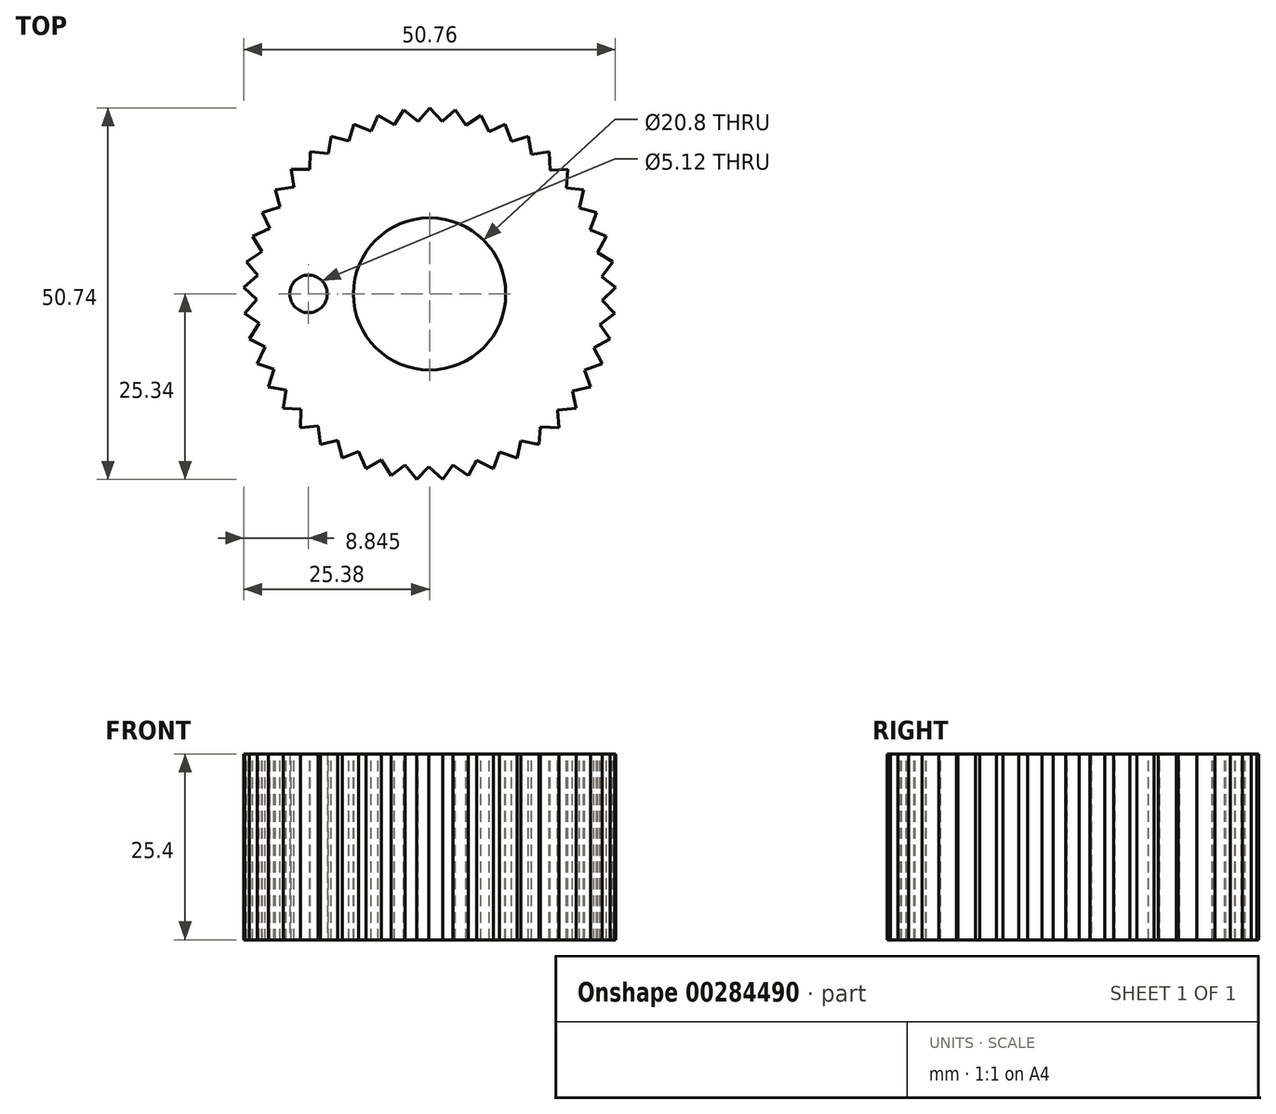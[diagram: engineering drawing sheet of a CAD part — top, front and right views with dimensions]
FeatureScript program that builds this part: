
annotation { "Feature Type Name" : "Feature", "Feature Type Description" : "" }
export const myFeature = defineFeature(function(context is Context, id is Id, definition is map)
    precondition{}
    {
        {
            var Q0;
            Q0=qCreatedBy(makeId("Top.planeOp"),FACE);
            var sketch = newSketch(context, id + "F0", { "sketchPlane" : qUnion([Q0])});
            skCircle(sketch, "E0", {"center": v(0, 0) * mm, "radius": 25.4 * mm});
            skSolve(sketch);
        }
        {
            var Q0;
            Q0=makeQuery(id+"F0.imprint","IMPRINT",FACE,{"disambiguationData":[TD([[makeQuery(id+"F0.imprint","IMPRINT",EDGE,{"derivedFrom":sQuery(id+"F0.wireOp",EDGE,"E0")}),1.0]])]});
            extrude(context, id + "F1", {"entities" : qUnion([Q0]), "depth" : 25.4 * mm});
        }
        {
            var Q0;
            Q0=makeQuery(id+"F1.opExtrude","CAP_FACE",FACE,{"disambiguationData":[OSD([sQuery(id+"F0.wireOp",EDGE,"E0")])],"isStart":false});
            var sketch = newSketch(context, id + "F2", { "sketchPlane" : qUnion([Q0])});
            skLineSegment(sketch, "E1", {"start": v(0, 0) * mm, "end": v(0, 49.68) * mm});
            skLineSegment(sketch, "E2", {"start": v(0, 24.84) * mm, "end": v(0, 25.4) * mm});
            skLineSegment(sketch, "E3", {"start": v(0, 25.4) * mm, "end": v(2.47, 22.76) * mm});
            skLineSegment(sketch, "E4", {"start": v(2.47, 22.76) * mm, "end": v(-2.23, 22.76) * mm});
            skLineSegment(sketch, "E5", {"start": v(-2.23, 22.76) * mm, "end": v(0, 25.4) * mm});
            skCircle(sketch, "E6.0", {"center": v(0, 0) * mm, "radius": 25.4 * mm});
            skLineSegment(sketch, "E7.1.1", {"start": v(-3.53, 25.15) * mm, "end": v(-0.72, 22.88) * mm});
            skLineSegment(sketch, "E7.1.2", {"start": v(-0.72, 22.88) * mm, "end": v(-5.38, 22.23) * mm});
            skLineSegment(sketch, "E7.1.3", {"start": v(-5.38, 22.23) * mm, "end": v(-3.53, 25.15) * mm});
            skLineSegment(sketch, "E7.2.1", {"start": v(-7, 24.42) * mm, "end": v(-3.9, 22.56) * mm});
            skLineSegment(sketch, "E7.2.2", {"start": v(-3.9, 22.56) * mm, "end": v(-8.42, 21.26) * mm});
            skLineSegment(sketch, "E7.2.3", {"start": v(-8.42, 21.26) * mm, "end": v(-7, 24.42) * mm});
            skLineSegment(sketch, "E8.2.3.0", {"start": v(-10.33, 23.2) * mm, "end": v(-7, 21.8) * mm});
            skLineSegment(sketch, "E8.5.3.0", {"start": v(-7, 21.8) * mm, "end": v(-11.3, 19.88) * mm});
            skLineSegment(sketch, "E8.8.3.0", {"start": v(-11.3, 19.88) * mm, "end": v(-10.33, 23.2) * mm});
            skLineSegment(sketch, "E8.2.4.0", {"start": v(-13.46, 21.54) * mm, "end": v(-9.96, 20.6) * mm});
            skLineSegment(sketch, "E8.5.4.0", {"start": v(-9.96, 20.6) * mm, "end": v(-13.96, 18.12) * mm});
            skLineSegment(sketch, "E8.8.4.0", {"start": v(-13.96, 18.12) * mm, "end": v(-13.46, 21.54) * mm});
            skLineSegment(sketch, "E8.2.5.0", {"start": v(-16.33, 19.46) * mm, "end": v(-12.74, 19.02) * mm});
            skLineSegment(sketch, "E8.5.5.0", {"start": v(-12.74, 19.02) * mm, "end": v(-16.34, 16) * mm});
            skLineSegment(sketch, "E8.8.5.0", {"start": v(-16.34, 16) * mm, "end": v(-16.33, 19.46) * mm});
            skLineSegment(sketch, "E8.2.6.0", {"start": v(-18.88, 17) * mm, "end": v(-15.26, 17.06) * mm});
            skLineSegment(sketch, "E8.5.6.0", {"start": v(-15.26, 17.06) * mm, "end": v(-18.4, 13.57) * mm});
            skLineSegment(sketch, "E8.8.6.0", {"start": v(-18.4, 13.57) * mm, "end": v(-18.88, 17) * mm});
            skLineSegment(sketch, "E8.2.7.0", {"start": v(-21.06, 14.2) * mm, "end": v(-17.49, 14.78) * mm});
            skLineSegment(sketch, "E8.5.7.0", {"start": v(-17.49, 14.78) * mm, "end": v(-20.12, 10.87) * mm});
            skLineSegment(sketch, "E8.8.7.0", {"start": v(-20.12, 10.87) * mm, "end": v(-21.06, 14.2) * mm});
            skLineSegment(sketch, "E8.2.8.0", {"start": v(-22.83, 11.13) * mm, "end": v(-19.37, 12.2) * mm});
            skLineSegment(sketch, "E8.5.8.0", {"start": v(-19.37, 12.2) * mm, "end": v(-21.43, 7.97) * mm});
            skLineSegment(sketch, "E8.8.8.0", {"start": v(-21.43, 7.97) * mm, "end": v(-22.83, 11.13) * mm});
            skLineSegment(sketch, "E8.2.9.0", {"start": v(-24.16, 7.85) * mm, "end": v(-20.88, 9.38) * mm});
            skLineSegment(sketch, "E8.5.9.0", {"start": v(-20.88, 9.38) * mm, "end": v(-22.34, 4.9) * mm});
            skLineSegment(sketch, "E8.8.9.0", {"start": v(-22.34, 4.9) * mm, "end": v(-24.16, 7.85) * mm});
            skLineSegment(sketch, "E8.2.10.0", {"start": v(-25.01, 4.41) * mm, "end": v(-21.98, 6.39) * mm});
            skLineSegment(sketch, "E8.5.10.0", {"start": v(-21.98, 6.39) * mm, "end": v(-22.8, 1.75) * mm});
            skLineSegment(sketch, "E8.8.10.0", {"start": v(-22.8, 1.75) * mm, "end": v(-25.01, 4.41) * mm});
            skLineSegment(sketch, "E8.2.11.0", {"start": v(-25.38, 0.89) * mm, "end": v(-22.66, 3.26) * mm});
            skLineSegment(sketch, "E8.5.11.0", {"start": v(-22.66, 3.26) * mm, "end": v(-22.82, -1.44) * mm});
            skLineSegment(sketch, "E8.8.11.0", {"start": v(-22.82, -1.44) * mm, "end": v(-25.38, 0.89) * mm});
            skLineSegment(sketch, "E8.2.12.0", {"start": v(-25.26, -2.66) * mm, "end": v(-22.9, 0.08) * mm});
            skLineSegment(sketch, "E8.5.12.0", {"start": v(-22.9, 0.08) * mm, "end": v(-22.4, -4.6) * mm});
            skLineSegment(sketch, "E8.8.12.0", {"start": v(-22.4, -4.6) * mm, "end": v(-25.26, -2.66) * mm});
            skLineSegment(sketch, "E8.2.13.0", {"start": v(-24.65, -6.14) * mm, "end": v(-22.68, -3.1) * mm});
            skLineSegment(sketch, "E8.5.13.0", {"start": v(-22.68, -3.1) * mm, "end": v(-21.54, -7.67) * mm});
            skLineSegment(sketch, "E8.8.13.0", {"start": v(-21.54, -7.67) * mm, "end": v(-24.65, -6.14) * mm});
            skLineSegment(sketch, "E8.2.14.0", {"start": v(-23.55, -9.52) * mm, "end": v(-22.03, -6.23) * mm});
            skLineSegment(sketch, "E8.5.14.0", {"start": v(-22.03, -6.23) * mm, "end": v(-20.26, -10.6) * mm});
            skLineSegment(sketch, "E8.8.14.0", {"start": v(-20.26, -10.6) * mm, "end": v(-23.55, -9.52) * mm});
            skLineSegment(sketch, "E8.2.15.0", {"start": v(-22, -12.7) * mm, "end": v(-20.95, -9.24) * mm});
            skLineSegment(sketch, "E8.5.15.0", {"start": v(-20.95, -9.24) * mm, "end": v(-18.6, -13.31) * mm});
            skLineSegment(sketch, "E8.8.15.0", {"start": v(-18.6, -13.31) * mm, "end": v(-22, -12.7) * mm});
            skLineSegment(sketch, "E8.2.16.0", {"start": v(-20.02, -15.64) * mm, "end": v(-19.46, -12.06) * mm});
            skLineSegment(sketch, "E8.5.16.0", {"start": v(-19.46, -12.06) * mm, "end": v(-16.56, -15.77) * mm});
            skLineSegment(sketch, "E8.8.16.0", {"start": v(-16.56, -15.77) * mm, "end": v(-20.02, -15.64) * mm});
            skLineSegment(sketch, "E8.2.17.0", {"start": v(-17.64, -18.27) * mm, "end": v(-17.59, -14.65) * mm});
            skLineSegment(sketch, "E8.5.17.0", {"start": v(-17.59, -14.65) * mm, "end": v(-14.2, -17.92) * mm});
            skLineSegment(sketch, "E8.8.17.0", {"start": v(-14.2, -17.92) * mm, "end": v(-17.64, -18.27) * mm});
            skLineSegment(sketch, "E8.2.18.0", {"start": v(-14.93, -20.55) * mm, "end": v(-15.38, -16.96) * mm});
            skLineSegment(sketch, "E8.5.18.0", {"start": v(-15.38, -16.96) * mm, "end": v(-11.57, -19.73) * mm});
            skLineSegment(sketch, "E8.8.18.0", {"start": v(-11.57, -19.73) * mm, "end": v(-14.93, -20.55) * mm});
            skLineSegment(sketch, "E8.2.19.0", {"start": v(-11.92, -22.43) * mm, "end": v(-12.87, -18.93) * mm});
            skLineSegment(sketch, "E8.5.19.0", {"start": v(-12.87, -18.93) * mm, "end": v(-8.71, -21.14) * mm});
            skLineSegment(sketch, "E8.8.19.0", {"start": v(-8.71, -21.14) * mm, "end": v(-11.92, -22.43) * mm});
            skLineSegment(sketch, "E8.2.20.0", {"start": v(-8.69, -23.87) * mm, "end": v(-10.1, -20.54) * mm});
            skLineSegment(sketch, "E8.5.20.0", {"start": v(-10.1, -20.54) * mm, "end": v(-5.68, -22.15) * mm});
            skLineSegment(sketch, "E8.8.20.0", {"start": v(-5.68, -22.15) * mm, "end": v(-8.69, -23.87) * mm});
            skLineSegment(sketch, "E8.2.21.0", {"start": v(-5.28, -24.84) * mm, "end": v(-7.15, -21.75) * mm});
            skLineSegment(sketch, "E8.5.21.0", {"start": v(-7.15, -21.75) * mm, "end": v(-2.55, -22.73) * mm});
            skLineSegment(sketch, "E8.8.21.0", {"start": v(-2.55, -22.73) * mm, "end": v(-5.28, -24.84) * mm});
            skLineSegment(sketch, "E8.2.22.0", {"start": v(-1.77, -25.34) * mm, "end": v(-4.05, -22.53) * mm});
            skLineSegment(sketch, "E8.5.22.0", {"start": v(-4.05, -22.53) * mm, "end": v(0.64, -22.86) * mm});
            skLineSegment(sketch, "E8.8.22.0", {"start": v(0.64, -22.86) * mm, "end": v(-1.77, -25.34) * mm});
            skLineSegment(sketch, "E8.2.23.0", {"start": v(1.77, -25.34) * mm, "end": v(-0.88, -22.88) * mm});
            skLineSegment(sketch, "E8.5.23.0", {"start": v(-0.88, -22.88) * mm, "end": v(3.82, -22.55) * mm});
            skLineSegment(sketch, "E8.8.23.0", {"start": v(3.82, -22.55) * mm, "end": v(1.77, -25.34) * mm});
            skLineSegment(sketch, "E8.2.24.0", {"start": v(5.28, -24.84) * mm, "end": v(2.31, -22.78) * mm});
            skLineSegment(sketch, "E8.5.24.0", {"start": v(2.31, -22.78) * mm, "end": v(6.92, -21.8) * mm});
            skLineSegment(sketch, "E8.8.24.0", {"start": v(6.92, -21.8) * mm, "end": v(5.28, -24.84) * mm});
            skLineSegment(sketch, "E8.2.25.0", {"start": v(8.69, -23.87) * mm, "end": v(5.46, -22.23) * mm});
            skLineSegment(sketch, "E8.5.25.0", {"start": v(5.46, -22.23) * mm, "end": v(9.88, -20.62) * mm});
            skLineSegment(sketch, "E8.8.25.0", {"start": v(9.88, -20.62) * mm, "end": v(8.69, -23.87) * mm});
            skLineSegment(sketch, "E8.2.26.0", {"start": v(11.92, -22.43) * mm, "end": v(8.5, -21.25) * mm});
            skLineSegment(sketch, "E8.5.26.0", {"start": v(8.5, -21.25) * mm, "end": v(12.66, -19.05) * mm});
            skLineSegment(sketch, "E8.8.26.0", {"start": v(12.66, -19.05) * mm, "end": v(11.92, -22.43) * mm});
            skLineSegment(sketch, "E8.2.27.0", {"start": v(14.93, -20.55) * mm, "end": v(11.38, -19.86) * mm});
            skLineSegment(sketch, "E8.5.27.0", {"start": v(11.38, -19.86) * mm, "end": v(15.19, -17.1) * mm});
            skLineSegment(sketch, "E8.8.27.0", {"start": v(15.19, -17.1) * mm, "end": v(14.93, -20.55) * mm});
            skLineSegment(sketch, "E8.2.28.0", {"start": v(17.64, -18.27) * mm, "end": v(14.03, -18.09) * mm});
            skLineSegment(sketch, "E8.5.28.0", {"start": v(14.03, -18.09) * mm, "end": v(17.42, -14.82) * mm});
            skLineSegment(sketch, "E8.8.28.0", {"start": v(17.42, -14.82) * mm, "end": v(17.64, -18.27) * mm});
            skLineSegment(sketch, "E8.2.29.0", {"start": v(20.02, -15.64) * mm, "end": v(16.41, -15.96) * mm});
            skLineSegment(sketch, "E8.5.29.0", {"start": v(16.41, -15.96) * mm, "end": v(19.3, -12.25) * mm});
            skLineSegment(sketch, "E8.8.29.0", {"start": v(19.3, -12.25) * mm, "end": v(20.02, -15.64) * mm});
            skLineSegment(sketch, "E8.2.30.0", {"start": v(22, -12.7) * mm, "end": v(18.47, -13.52) * mm});
            skLineSegment(sketch, "E8.5.30.0", {"start": v(18.47, -13.52) * mm, "end": v(20.83, -9.44) * mm});
            skLineSegment(sketch, "E8.8.30.0", {"start": v(20.83, -9.44) * mm, "end": v(22, -12.7) * mm});
            skLineSegment(sketch, "E8.2.31.0", {"start": v(23.55, -9.52) * mm, "end": v(20.18, -10.82) * mm});
            skLineSegment(sketch, "E8.5.31.0", {"start": v(20.18, -10.82) * mm, "end": v(21.94, -6.45) * mm});
            skLineSegment(sketch, "E8.8.31.0", {"start": v(21.94, -6.45) * mm, "end": v(23.55, -9.52) * mm});
            skLineSegment(sketch, "E8.2.32.0", {"start": v(24.65, -6.14) * mm, "end": v(21.48, -7.9) * mm});
            skLineSegment(sketch, "E8.5.32.0", {"start": v(21.48, -7.9) * mm, "end": v(22.62, -3.34) * mm});
            skLineSegment(sketch, "E8.8.32.0", {"start": v(22.62, -3.34) * mm, "end": v(24.65, -6.14) * mm});
            skLineSegment(sketch, "E8.2.33.0", {"start": v(25.26, -2.66) * mm, "end": v(22.38, -4.84) * mm});
            skLineSegment(sketch, "E8.5.33.0", {"start": v(22.38, -4.84) * mm, "end": v(22.87, -0.16) * mm});
            skLineSegment(sketch, "E8.8.33.0", {"start": v(22.87, -0.16) * mm, "end": v(25.26, -2.66) * mm});
            skLineSegment(sketch, "E8.2.34.0", {"start": v(25.38, 0.89) * mm, "end": v(22.83, -1.68) * mm});
            skLineSegment(sketch, "E8.5.34.0", {"start": v(22.83, -1.68) * mm, "end": v(22.67, 3.03) * mm});
            skLineSegment(sketch, "E8.8.34.0", {"start": v(22.67, 3.03) * mm, "end": v(25.38, 0.89) * mm});
            skLineSegment(sketch, "E8.2.35.0", {"start": v(25.01, 4.41) * mm, "end": v(22.84, 1.52) * mm});
            skLineSegment(sketch, "E8.5.35.0", {"start": v(22.84, 1.52) * mm, "end": v(22.02, 6.15) * mm});
            skLineSegment(sketch, "E8.8.35.0", {"start": v(22.02, 6.15) * mm, "end": v(25.01, 4.41) * mm});
            skLineSegment(sketch, "E8.2.36.0", {"start": v(24.16, 7.85) * mm, "end": v(22.4, 4.68) * mm});
            skLineSegment(sketch, "E8.5.36.0", {"start": v(22.4, 4.68) * mm, "end": v(20.95, 9.16) * mm});
            skLineSegment(sketch, "E8.8.36.0", {"start": v(20.95, 9.16) * mm, "end": v(24.16, 7.85) * mm});
            skLineSegment(sketch, "E8.2.37.0", {"start": v(22.83, 11.13) * mm, "end": v(21.54, 7.76) * mm});
            skLineSegment(sketch, "E8.5.37.0", {"start": v(21.54, 7.76) * mm, "end": v(19.48, 11.99) * mm});
            skLineSegment(sketch, "E8.8.37.0", {"start": v(19.48, 11.99) * mm, "end": v(22.83, 11.13) * mm});
            skLineSegment(sketch, "E8.2.38.0", {"start": v(21.06, 14.2) * mm, "end": v(20.25, 10.68) * mm});
            skLineSegment(sketch, "E8.5.38.0", {"start": v(20.25, 10.68) * mm, "end": v(17.62, 14.58) * mm});
            skLineSegment(sketch, "E8.8.38.0", {"start": v(17.62, 14.58) * mm, "end": v(21.06, 14.2) * mm});
            skLineSegment(sketch, "E8.2.39.0", {"start": v(18.88, 17) * mm, "end": v(18.57, 13.4) * mm});
            skLineSegment(sketch, "E8.5.39.0", {"start": v(18.57, 13.4) * mm, "end": v(15.42, 16.89) * mm});
            skLineSegment(sketch, "E8.8.39.0", {"start": v(15.42, 16.89) * mm, "end": v(18.88, 17) * mm});
            skLineSegment(sketch, "E8.2.40.0", {"start": v(16.33, 19.46) * mm, "end": v(16.52, 15.85) * mm});
            skLineSegment(sketch, "E8.5.40.0", {"start": v(16.52, 15.85) * mm, "end": v(12.92, 18.87) * mm});
            skLineSegment(sketch, "E8.8.40.0", {"start": v(12.92, 18.87) * mm, "end": v(16.33, 19.46) * mm});
            skLineSegment(sketch, "E8.2.41.0", {"start": v(13.46, 21.54) * mm, "end": v(14.16, 18) * mm});
            skLineSegment(sketch, "E8.5.41.0", {"start": v(14.16, 18) * mm, "end": v(10.17, 20.48) * mm});
            skLineSegment(sketch, "E8.8.41.0", {"start": v(10.17, 20.48) * mm, "end": v(13.46, 21.54) * mm});
            skLineSegment(sketch, "E8.2.42.0", {"start": v(10.33, 23.2) * mm, "end": v(11.51, 19.79) * mm});
            skLineSegment(sketch, "E8.5.42.0", {"start": v(11.51, 19.79) * mm, "end": v(7.22, 21.7) * mm});
            skLineSegment(sketch, "E8.8.42.0", {"start": v(7.22, 21.7) * mm, "end": v(10.33, 23.2) * mm});
            skLineSegment(sketch, "E8.2.43.0", {"start": v(7, 24.42) * mm, "end": v(8.65, 21.2) * mm});
            skLineSegment(sketch, "E8.5.43.0", {"start": v(8.65, 21.2) * mm, "end": v(4.12, 22.5) * mm});
            skLineSegment(sketch, "E8.8.43.0", {"start": v(4.12, 22.5) * mm, "end": v(7, 24.42) * mm});
            skLineSegment(sketch, "E8.2.44.0", {"start": v(3.53, 25.15) * mm, "end": v(5.61, 22.2) * mm});
            skLineSegment(sketch, "E8.5.44.0", {"start": v(5.61, 22.2) * mm, "end": v(0.95, 22.85) * mm});
            skLineSegment(sketch, "E8.8.44.0", {"start": v(0.95, 22.85) * mm, "end": v(3.53, 25.15) * mm});
            skCircle(sketch, "E9", {"center": v(0, 0) * mm, "radius": 10.4 * mm});
            skSolve(sketch);
        }
        {
            var Q0;
            {var subQ1=sQuery(id+"F2.wireOp",EDGE,"E8.8.21.0");var subQ3=sQuery(id+"F2.wireOp",EDGE,"E8.2.22.0");var subQ4=makeQuery(id+"F2.imprint","INTERSECT",VERTEX,{"derivedFrom":[subQ1,subQ3]});Q0=makeQuery(id+"F2.imprint","IMPRINT",FACE,{"disambiguationData":[TD([[makeQuery(id+"F2.imprint","IMPRINT",EDGE,{"disambiguationData":[TD([[subQ4,-1.0]])],"derivedFrom":subQ1}),1.0]])]});}
            var Q1;
            {var subQ1=sQuery(id+"F2.wireOp",EDGE,"E8.8.22.0");var subQ3=sQuery(id+"F2.wireOp",EDGE,"E8.2.23.0");var subQ4=makeQuery(id+"F2.imprint","INTERSECT",VERTEX,{"derivedFrom":[subQ1,subQ3]});Q1=makeQuery(id+"F2.imprint","IMPRINT",FACE,{"disambiguationData":[TD([[makeQuery(id+"F2.imprint","IMPRINT",EDGE,{"disambiguationData":[TD([[subQ4,-1.0]])],"derivedFrom":subQ1}),1.0]])]});}
            var Q2;
            {var subQ1=sQuery(id+"F2.wireOp",EDGE,"E8.8.23.0");var subQ3=sQuery(id+"F2.wireOp",EDGE,"E8.2.24.0");var subQ4=makeQuery(id+"F2.imprint","INTERSECT",VERTEX,{"derivedFrom":[subQ1,subQ3]});Q2=makeQuery(id+"F2.imprint","IMPRINT",FACE,{"disambiguationData":[TD([[makeQuery(id+"F2.imprint","IMPRINT",EDGE,{"disambiguationData":[TD([[subQ4,-1.0]])],"derivedFrom":subQ1}),1.0]])]});}
            var Q3;
            {var subQ1=sQuery(id+"F2.wireOp",EDGE,"E8.8.24.0");var subQ3=sQuery(id+"F2.wireOp",EDGE,"E8.2.25.0");var subQ4=makeQuery(id+"F2.imprint","INTERSECT",VERTEX,{"derivedFrom":[subQ1,subQ3]});Q3=makeQuery(id+"F2.imprint","IMPRINT",FACE,{"disambiguationData":[TD([[makeQuery(id+"F2.imprint","IMPRINT",EDGE,{"disambiguationData":[TD([[subQ4,-1.0]])],"derivedFrom":subQ1}),1.0]])]});}
            var Q4;
            {var subQ1=sQuery(id+"F2.wireOp",EDGE,"E8.8.25.0");var subQ3=sQuery(id+"F2.wireOp",EDGE,"E8.2.26.0");var subQ4=makeQuery(id+"F2.imprint","INTERSECT",VERTEX,{"derivedFrom":[subQ1,subQ3]});Q4=makeQuery(id+"F2.imprint","IMPRINT",FACE,{"disambiguationData":[TD([[makeQuery(id+"F2.imprint","IMPRINT",EDGE,{"disambiguationData":[TD([[subQ4,-1.0]])],"derivedFrom":subQ1}),1.0]])]});}
            var Q5;
            {var subQ1=sQuery(id+"F2.wireOp",EDGE,"E8.8.26.0");var subQ3=sQuery(id+"F2.wireOp",EDGE,"E8.2.27.0");var subQ4=makeQuery(id+"F2.imprint","INTERSECT",VERTEX,{"derivedFrom":[subQ1,subQ3]});Q5=makeQuery(id+"F2.imprint","IMPRINT",FACE,{"disambiguationData":[TD([[makeQuery(id+"F2.imprint","IMPRINT",EDGE,{"disambiguationData":[TD([[subQ4,-1.0]])],"derivedFrom":subQ1}),1.0]])]});}
            var Q6;
            {var subQ1=sQuery(id+"F2.wireOp",EDGE,"E8.8.27.0");var subQ3=sQuery(id+"F2.wireOp",EDGE,"E8.2.28.0");var subQ4=makeQuery(id+"F2.imprint","INTERSECT",VERTEX,{"derivedFrom":[subQ1,subQ3]});Q6=makeQuery(id+"F2.imprint","IMPRINT",FACE,{"disambiguationData":[TD([[makeQuery(id+"F2.imprint","IMPRINT",EDGE,{"disambiguationData":[TD([[subQ4,-1.0]])],"derivedFrom":subQ1}),1.0]])]});}
            var Q7;
            {var subQ1=sQuery(id+"F2.wireOp",EDGE,"E8.8.28.0");var subQ3=sQuery(id+"F2.wireOp",EDGE,"E8.2.29.0");var subQ4=makeQuery(id+"F2.imprint","INTERSECT",VERTEX,{"derivedFrom":[subQ1,subQ3]});Q7=makeQuery(id+"F2.imprint","IMPRINT",FACE,{"disambiguationData":[TD([[makeQuery(id+"F2.imprint","IMPRINT",EDGE,{"disambiguationData":[TD([[subQ4,-1.0]])],"derivedFrom":subQ1}),1.0]])]});}
            var Q8;
            {var subQ1=sQuery(id+"F2.wireOp",EDGE,"E8.8.29.0");var subQ3=sQuery(id+"F2.wireOp",EDGE,"E8.2.30.0");var subQ4=makeQuery(id+"F2.imprint","INTERSECT",VERTEX,{"derivedFrom":[subQ1,subQ3]});Q8=makeQuery(id+"F2.imprint","IMPRINT",FACE,{"disambiguationData":[TD([[makeQuery(id+"F2.imprint","IMPRINT",EDGE,{"disambiguationData":[TD([[subQ4,-1.0]])],"derivedFrom":subQ1}),1.0]])]});}
            var Q9;
            {var subQ1=sQuery(id+"F2.wireOp",EDGE,"E8.8.30.0");var subQ3=sQuery(id+"F2.wireOp",EDGE,"E8.2.31.0");var subQ4=makeQuery(id+"F2.imprint","INTERSECT",VERTEX,{"derivedFrom":[subQ1,subQ3]});Q9=makeQuery(id+"F2.imprint","IMPRINT",FACE,{"disambiguationData":[TD([[makeQuery(id+"F2.imprint","IMPRINT",EDGE,{"disambiguationData":[TD([[subQ4,-1.0]])],"derivedFrom":subQ1}),1.0]])]});}
            var Q10;
            {var subQ1=sQuery(id+"F2.wireOp",EDGE,"E8.8.31.0");var subQ3=sQuery(id+"F2.wireOp",EDGE,"E8.2.32.0");var subQ4=makeQuery(id+"F2.imprint","INTERSECT",VERTEX,{"derivedFrom":[subQ1,subQ3]});Q10=makeQuery(id+"F2.imprint","IMPRINT",FACE,{"disambiguationData":[TD([[makeQuery(id+"F2.imprint","IMPRINT",EDGE,{"disambiguationData":[TD([[subQ4,-1.0]])],"derivedFrom":subQ1}),1.0]])]});}
            var Q11;
            {var subQ1=sQuery(id+"F2.wireOp",EDGE,"E8.8.32.0");var subQ3=sQuery(id+"F2.wireOp",EDGE,"E8.2.33.0");var subQ4=makeQuery(id+"F2.imprint","INTERSECT",VERTEX,{"derivedFrom":[subQ1,subQ3]});Q11=makeQuery(id+"F2.imprint","IMPRINT",FACE,{"disambiguationData":[TD([[makeQuery(id+"F2.imprint","IMPRINT",EDGE,{"disambiguationData":[TD([[subQ4,-1.0]])],"derivedFrom":subQ1}),1.0]])]});}
            var Q12;
            {var subQ1=sQuery(id+"F2.wireOp",EDGE,"E8.8.33.0");var subQ3=sQuery(id+"F2.wireOp",EDGE,"E8.2.34.0");var subQ4=makeQuery(id+"F2.imprint","INTERSECT",VERTEX,{"derivedFrom":[subQ1,subQ3]});Q12=makeQuery(id+"F2.imprint","IMPRINT",FACE,{"disambiguationData":[TD([[makeQuery(id+"F2.imprint","IMPRINT",EDGE,{"disambiguationData":[TD([[subQ4,-1.0]])],"derivedFrom":subQ1}),1.0]])]});}
            var Q13;
            {var subQ1=sQuery(id+"F2.wireOp",EDGE,"E8.8.34.0");var subQ3=sQuery(id+"F2.wireOp",EDGE,"E8.2.35.0");var subQ4=makeQuery(id+"F2.imprint","INTERSECT",VERTEX,{"derivedFrom":[subQ1,subQ3]});Q13=makeQuery(id+"F2.imprint","IMPRINT",FACE,{"disambiguationData":[TD([[makeQuery(id+"F2.imprint","IMPRINT",EDGE,{"disambiguationData":[TD([[subQ4,-1.0]])],"derivedFrom":subQ1}),1.0]])]});}
            var Q14;
            {var subQ1=sQuery(id+"F2.wireOp",EDGE,"E8.8.35.0");var subQ3=sQuery(id+"F2.wireOp",EDGE,"E8.2.36.0");var subQ4=makeQuery(id+"F2.imprint","INTERSECT",VERTEX,{"derivedFrom":[subQ1,subQ3]});Q14=makeQuery(id+"F2.imprint","IMPRINT",FACE,{"disambiguationData":[TD([[makeQuery(id+"F2.imprint","IMPRINT",EDGE,{"disambiguationData":[TD([[subQ4,-1.0]])],"derivedFrom":subQ1}),1.0]])]});}
            var Q15;
            {var subQ1=sQuery(id+"F2.wireOp",EDGE,"E8.8.36.0");var subQ3=sQuery(id+"F2.wireOp",EDGE,"E8.2.37.0");var subQ4=makeQuery(id+"F2.imprint","INTERSECT",VERTEX,{"derivedFrom":[subQ1,subQ3]});Q15=makeQuery(id+"F2.imprint","IMPRINT",FACE,{"disambiguationData":[TD([[makeQuery(id+"F2.imprint","IMPRINT",EDGE,{"disambiguationData":[TD([[subQ4,-1.0]])],"derivedFrom":subQ1}),1.0]])]});}
            var Q16;
            {var subQ1=sQuery(id+"F2.wireOp",EDGE,"E8.8.37.0");var subQ3=sQuery(id+"F2.wireOp",EDGE,"E8.2.38.0");var subQ4=makeQuery(id+"F2.imprint","INTERSECT",VERTEX,{"derivedFrom":[subQ1,subQ3]});Q16=makeQuery(id+"F2.imprint","IMPRINT",FACE,{"disambiguationData":[TD([[makeQuery(id+"F2.imprint","IMPRINT",EDGE,{"disambiguationData":[TD([[subQ4,-1.0]])],"derivedFrom":subQ1}),1.0]])]});}
            var Q17;
            {var subQ1=sQuery(id+"F2.wireOp",EDGE,"E8.8.38.0");var subQ3=sQuery(id+"F2.wireOp",EDGE,"E8.2.39.0");var subQ4=makeQuery(id+"F2.imprint","INTERSECT",VERTEX,{"derivedFrom":[subQ1,subQ3]});Q17=makeQuery(id+"F2.imprint","IMPRINT",FACE,{"disambiguationData":[TD([[makeQuery(id+"F2.imprint","IMPRINT",EDGE,{"disambiguationData":[TD([[subQ4,-1.0]])],"derivedFrom":subQ1}),1.0]])]});}
            var Q18;
            {var subQ1=sQuery(id+"F2.wireOp",EDGE,"E8.8.39.0");var subQ3=sQuery(id+"F2.wireOp",EDGE,"E8.2.40.0");var subQ4=makeQuery(id+"F2.imprint","INTERSECT",VERTEX,{"derivedFrom":[subQ1,subQ3]});Q18=makeQuery(id+"F2.imprint","IMPRINT",FACE,{"disambiguationData":[TD([[makeQuery(id+"F2.imprint","IMPRINT",EDGE,{"disambiguationData":[TD([[subQ4,-1.0]])],"derivedFrom":subQ1}),1.0]])]});}
            var Q19;
            {var subQ1=sQuery(id+"F2.wireOp",EDGE,"E8.8.40.0");var subQ3=sQuery(id+"F2.wireOp",EDGE,"E8.2.41.0");var subQ4=makeQuery(id+"F2.imprint","INTERSECT",VERTEX,{"derivedFrom":[subQ1,subQ3]});Q19=makeQuery(id+"F2.imprint","IMPRINT",FACE,{"disambiguationData":[TD([[makeQuery(id+"F2.imprint","IMPRINT",EDGE,{"disambiguationData":[TD([[subQ4,-1.0]])],"derivedFrom":subQ1}),1.0]])]});}
            var Q20;
            {var subQ1=sQuery(id+"F2.wireOp",EDGE,"E8.8.41.0");var subQ3=sQuery(id+"F2.wireOp",EDGE,"E8.2.42.0");var subQ4=makeQuery(id+"F2.imprint","INTERSECT",VERTEX,{"derivedFrom":[subQ1,subQ3]});Q20=makeQuery(id+"F2.imprint","IMPRINT",FACE,{"disambiguationData":[TD([[makeQuery(id+"F2.imprint","IMPRINT",EDGE,{"disambiguationData":[TD([[subQ4,-1.0]])],"derivedFrom":subQ1}),1.0]])]});}
            var Q21;
            {var subQ1=sQuery(id+"F2.wireOp",EDGE,"E8.8.42.0");var subQ3=sQuery(id+"F2.wireOp",EDGE,"E8.2.43.0");var subQ4=makeQuery(id+"F2.imprint","INTERSECT",VERTEX,{"derivedFrom":[subQ1,subQ3]});Q21=makeQuery(id+"F2.imprint","IMPRINT",FACE,{"disambiguationData":[TD([[makeQuery(id+"F2.imprint","IMPRINT",EDGE,{"disambiguationData":[TD([[subQ4,-1.0]])],"derivedFrom":subQ1}),1.0]])]});}
            var Q22;
            {var subQ1=sQuery(id+"F2.wireOp",EDGE,"E8.8.43.0");var subQ3=sQuery(id+"F2.wireOp",EDGE,"E8.2.44.0");var subQ4=makeQuery(id+"F2.imprint","INTERSECT",VERTEX,{"derivedFrom":[subQ1,subQ3]});Q22=makeQuery(id+"F2.imprint","IMPRINT",FACE,{"disambiguationData":[TD([[makeQuery(id+"F2.imprint","IMPRINT",EDGE,{"disambiguationData":[TD([[subQ4,-1.0]])],"derivedFrom":subQ1}),1.0]])]});}
            var Q23;
            {var subQ1=sQuery(id+"F2.wireOp",EDGE,"E3");var subQ3=sQuery(id+"F2.wireOp",EDGE,"E8.8.44.0");var subQ4=makeQuery(id+"F2.imprint","INTERSECT",VERTEX,{"derivedFrom":[subQ1,subQ3]});Q23=makeQuery(id+"F2.imprint","IMPRINT",FACE,{"disambiguationData":[TD([[makeQuery(id+"F2.imprint","IMPRINT",EDGE,{"disambiguationData":[TD([[subQ4,-1.0]])],"derivedFrom":subQ3}),1.0]])]});}
            var Q24;
            {var subQ1=sQuery(id+"F2.wireOp",EDGE,"E5");var subQ3=sQuery(id+"F2.wireOp",EDGE,"E7.1.1");var subQ4=makeQuery(id+"F2.imprint","INTERSECT",VERTEX,{"derivedFrom":[subQ1,subQ3]});Q24=makeQuery(id+"F2.imprint","IMPRINT",FACE,{"disambiguationData":[TD([[makeQuery(id+"F2.imprint","IMPRINT",EDGE,{"disambiguationData":[TD([[subQ4,1.0]])],"derivedFrom":subQ3}),1.0]])]});}
            var Q25;
            {var subQ1=sQuery(id+"F2.wireOp",EDGE,"E7.1.3");var subQ3=sQuery(id+"F2.wireOp",EDGE,"E7.2.1");var subQ4=makeQuery(id+"F2.imprint","INTERSECT",VERTEX,{"derivedFrom":[subQ1,subQ3]});Q25=makeQuery(id+"F2.imprint","IMPRINT",FACE,{"disambiguationData":[TD([[makeQuery(id+"F2.imprint","IMPRINT",EDGE,{"disambiguationData":[TD([[subQ4,-1.0]])],"derivedFrom":subQ1}),1.0]])]});}
            var Q26;
            {var subQ1=sQuery(id+"F2.wireOp",EDGE,"E7.2.3");var subQ3=sQuery(id+"F2.wireOp",EDGE,"E8.2.3.0");var subQ4=makeQuery(id+"F2.imprint","INTERSECT",VERTEX,{"derivedFrom":[subQ1,subQ3]});Q26=makeQuery(id+"F2.imprint","IMPRINT",FACE,{"disambiguationData":[TD([[makeQuery(id+"F2.imprint","IMPRINT",EDGE,{"disambiguationData":[TD([[subQ4,-1.0]])],"derivedFrom":subQ1}),1.0]])]});}
            var Q27;
            {var subQ1=sQuery(id+"F2.wireOp",EDGE,"E8.8.3.0");var subQ3=sQuery(id+"F2.wireOp",EDGE,"E8.2.4.0");var subQ4=makeQuery(id+"F2.imprint","INTERSECT",VERTEX,{"derivedFrom":[subQ1,subQ3]});Q27=makeQuery(id+"F2.imprint","IMPRINT",FACE,{"disambiguationData":[TD([[makeQuery(id+"F2.imprint","IMPRINT",EDGE,{"disambiguationData":[TD([[subQ4,-1.0]])],"derivedFrom":subQ1}),1.0]])]});}
            var Q28;
            {var subQ1=sQuery(id+"F2.wireOp",EDGE,"E8.8.4.0");var subQ3=sQuery(id+"F2.wireOp",EDGE,"E8.2.5.0");var subQ4=makeQuery(id+"F2.imprint","INTERSECT",VERTEX,{"derivedFrom":[subQ1,subQ3]});Q28=makeQuery(id+"F2.imprint","IMPRINT",FACE,{"disambiguationData":[TD([[makeQuery(id+"F2.imprint","IMPRINT",EDGE,{"disambiguationData":[TD([[subQ4,-1.0]])],"derivedFrom":subQ1}),1.0]])]});}
            var Q29;
            {var subQ1=sQuery(id+"F2.wireOp",EDGE,"E8.8.5.0");var subQ3=sQuery(id+"F2.wireOp",EDGE,"E8.2.6.0");var subQ4=makeQuery(id+"F2.imprint","INTERSECT",VERTEX,{"derivedFrom":[subQ1,subQ3]});Q29=makeQuery(id+"F2.imprint","IMPRINT",FACE,{"disambiguationData":[TD([[makeQuery(id+"F2.imprint","IMPRINT",EDGE,{"disambiguationData":[TD([[subQ4,-1.0]])],"derivedFrom":subQ1}),1.0]])]});}
            var Q30;
            {var subQ1=sQuery(id+"F2.wireOp",EDGE,"E8.8.6.0");var subQ3=sQuery(id+"F2.wireOp",EDGE,"E8.2.7.0");var subQ4=makeQuery(id+"F2.imprint","INTERSECT",VERTEX,{"derivedFrom":[subQ1,subQ3]});Q30=makeQuery(id+"F2.imprint","IMPRINT",FACE,{"disambiguationData":[TD([[makeQuery(id+"F2.imprint","IMPRINT",EDGE,{"disambiguationData":[TD([[subQ4,-1.0]])],"derivedFrom":subQ1}),1.0]])]});}
            var Q31;
            {var subQ1=sQuery(id+"F2.wireOp",EDGE,"E8.8.7.0");var subQ3=sQuery(id+"F2.wireOp",EDGE,"E8.2.8.0");var subQ4=makeQuery(id+"F2.imprint","INTERSECT",VERTEX,{"derivedFrom":[subQ1,subQ3]});Q31=makeQuery(id+"F2.imprint","IMPRINT",FACE,{"disambiguationData":[TD([[makeQuery(id+"F2.imprint","IMPRINT",EDGE,{"disambiguationData":[TD([[subQ4,-1.0]])],"derivedFrom":subQ1}),1.0]])]});}
            var Q32;
            {var subQ1=sQuery(id+"F2.wireOp",EDGE,"E8.8.8.0");var subQ3=sQuery(id+"F2.wireOp",EDGE,"E8.2.9.0");var subQ4=makeQuery(id+"F2.imprint","INTERSECT",VERTEX,{"derivedFrom":[subQ1,subQ3]});Q32=makeQuery(id+"F2.imprint","IMPRINT",FACE,{"disambiguationData":[TD([[makeQuery(id+"F2.imprint","IMPRINT",EDGE,{"disambiguationData":[TD([[subQ4,-1.0]])],"derivedFrom":subQ1}),1.0]])]});}
            var Q33;
            {var subQ1=sQuery(id+"F2.wireOp",EDGE,"E8.8.9.0");var subQ3=sQuery(id+"F2.wireOp",EDGE,"E8.2.10.0");var subQ4=makeQuery(id+"F2.imprint","INTERSECT",VERTEX,{"derivedFrom":[subQ1,subQ3]});Q33=makeQuery(id+"F2.imprint","IMPRINT",FACE,{"disambiguationData":[TD([[makeQuery(id+"F2.imprint","IMPRINT",EDGE,{"disambiguationData":[TD([[subQ4,-1.0]])],"derivedFrom":subQ1}),1.0]])]});}
            var Q34;
            {var subQ1=sQuery(id+"F2.wireOp",EDGE,"E8.8.10.0");var subQ3=sQuery(id+"F2.wireOp",EDGE,"E8.2.11.0");var subQ4=makeQuery(id+"F2.imprint","INTERSECT",VERTEX,{"derivedFrom":[subQ1,subQ3]});Q34=makeQuery(id+"F2.imprint","IMPRINT",FACE,{"disambiguationData":[TD([[makeQuery(id+"F2.imprint","IMPRINT",EDGE,{"disambiguationData":[TD([[subQ4,-1.0]])],"derivedFrom":subQ1}),1.0]])]});}
            var Q35;
            {var subQ1=sQuery(id+"F2.wireOp",EDGE,"E8.8.11.0");var subQ3=sQuery(id+"F2.wireOp",EDGE,"E8.2.12.0");var subQ4=makeQuery(id+"F2.imprint","INTERSECT",VERTEX,{"derivedFrom":[subQ1,subQ3]});Q35=makeQuery(id+"F2.imprint","IMPRINT",FACE,{"disambiguationData":[TD([[makeQuery(id+"F2.imprint","IMPRINT",EDGE,{"disambiguationData":[TD([[subQ4,-1.0]])],"derivedFrom":subQ1}),1.0]])]});}
            var Q36;
            {var subQ1=sQuery(id+"F2.wireOp",EDGE,"E8.8.12.0");var subQ3=sQuery(id+"F2.wireOp",EDGE,"E8.2.13.0");var subQ4=makeQuery(id+"F2.imprint","INTERSECT",VERTEX,{"derivedFrom":[subQ1,subQ3]});Q36=makeQuery(id+"F2.imprint","IMPRINT",FACE,{"disambiguationData":[TD([[makeQuery(id+"F2.imprint","IMPRINT",EDGE,{"disambiguationData":[TD([[subQ4,-1.0]])],"derivedFrom":subQ1}),1.0]])]});}
            var Q37;
            {var subQ1=sQuery(id+"F2.wireOp",EDGE,"E8.8.13.0");var subQ3=sQuery(id+"F2.wireOp",EDGE,"E8.2.14.0");var subQ4=makeQuery(id+"F2.imprint","INTERSECT",VERTEX,{"derivedFrom":[subQ1,subQ3]});Q37=makeQuery(id+"F2.imprint","IMPRINT",FACE,{"disambiguationData":[TD([[makeQuery(id+"F2.imprint","IMPRINT",EDGE,{"disambiguationData":[TD([[subQ4,-1.0]])],"derivedFrom":subQ1}),1.0]])]});}
            var Q38;
            {var subQ1=sQuery(id+"F2.wireOp",EDGE,"E8.8.14.0");var subQ3=sQuery(id+"F2.wireOp",EDGE,"E8.2.15.0");var subQ4=makeQuery(id+"F2.imprint","INTERSECT",VERTEX,{"derivedFrom":[subQ1,subQ3]});Q38=makeQuery(id+"F2.imprint","IMPRINT",FACE,{"disambiguationData":[TD([[makeQuery(id+"F2.imprint","IMPRINT",EDGE,{"disambiguationData":[TD([[subQ4,-1.0]])],"derivedFrom":subQ1}),1.0]])]});}
            var Q39;
            {var subQ1=sQuery(id+"F2.wireOp",EDGE,"E8.8.15.0");var subQ3=sQuery(id+"F2.wireOp",EDGE,"E8.2.16.0");var subQ4=makeQuery(id+"F2.imprint","INTERSECT",VERTEX,{"derivedFrom":[subQ1,subQ3]});Q39=makeQuery(id+"F2.imprint","IMPRINT",FACE,{"disambiguationData":[TD([[makeQuery(id+"F2.imprint","IMPRINT",EDGE,{"disambiguationData":[TD([[subQ4,-1.0]])],"derivedFrom":subQ1}),1.0]])]});}
            var Q40;
            {var subQ1=sQuery(id+"F2.wireOp",EDGE,"E8.8.16.0");var subQ3=sQuery(id+"F2.wireOp",EDGE,"E8.2.17.0");var subQ4=makeQuery(id+"F2.imprint","INTERSECT",VERTEX,{"derivedFrom":[subQ1,subQ3]});Q40=makeQuery(id+"F2.imprint","IMPRINT",FACE,{"disambiguationData":[TD([[makeQuery(id+"F2.imprint","IMPRINT",EDGE,{"disambiguationData":[TD([[subQ4,-1.0]])],"derivedFrom":subQ1}),1.0]])]});}
            var Q41;
            {var subQ1=sQuery(id+"F2.wireOp",EDGE,"E8.8.17.0");var subQ3=sQuery(id+"F2.wireOp",EDGE,"E8.2.18.0");var subQ4=makeQuery(id+"F2.imprint","INTERSECT",VERTEX,{"derivedFrom":[subQ1,subQ3]});Q41=makeQuery(id+"F2.imprint","IMPRINT",FACE,{"disambiguationData":[TD([[makeQuery(id+"F2.imprint","IMPRINT",EDGE,{"disambiguationData":[TD([[subQ4,-1.0]])],"derivedFrom":subQ1}),1.0]])]});}
            var Q42;
            {var subQ1=sQuery(id+"F2.wireOp",EDGE,"E8.8.18.0");var subQ3=sQuery(id+"F2.wireOp",EDGE,"E8.2.19.0");var subQ4=makeQuery(id+"F2.imprint","INTERSECT",VERTEX,{"derivedFrom":[subQ1,subQ3]});Q42=makeQuery(id+"F2.imprint","IMPRINT",FACE,{"disambiguationData":[TD([[makeQuery(id+"F2.imprint","IMPRINT",EDGE,{"disambiguationData":[TD([[subQ4,-1.0]])],"derivedFrom":subQ1}),1.0]])]});}
            var Q43;
            {var subQ1=sQuery(id+"F2.wireOp",EDGE,"E8.8.19.0");var subQ3=sQuery(id+"F2.wireOp",EDGE,"E8.2.20.0");var subQ4=makeQuery(id+"F2.imprint","INTERSECT",VERTEX,{"derivedFrom":[subQ1,subQ3]});Q43=makeQuery(id+"F2.imprint","IMPRINT",FACE,{"disambiguationData":[TD([[makeQuery(id+"F2.imprint","IMPRINT",EDGE,{"disambiguationData":[TD([[subQ4,-1.0]])],"derivedFrom":subQ1}),1.0]])]});}
            var Q44;
            {var subQ1=sQuery(id+"F2.wireOp",EDGE,"E8.8.20.0");var subQ3=sQuery(id+"F2.wireOp",EDGE,"E8.2.21.0");var subQ4=makeQuery(id+"F2.imprint","INTERSECT",VERTEX,{"derivedFrom":[subQ1,subQ3]});Q44=makeQuery(id+"F2.imprint","IMPRINT",FACE,{"disambiguationData":[TD([[makeQuery(id+"F2.imprint","IMPRINT",EDGE,{"disambiguationData":[TD([[subQ4,-1.0]])],"derivedFrom":subQ1}),1.0]])]});}
            extrude(context, id + "F3", {"entities" : qUnion([Q0, Q1, Q2, Q3, Q4, Q5, Q6, Q7, Q8, Q9, Q10, Q11, Q12, Q13, Q14, Q15, Q16, Q17, Q18, Q19, Q20, Q21, Q22, Q23, Q24, Q25, Q26, Q27, Q28, Q29, Q30, Q31, Q32, Q33, Q34, Q35, Q36, Q37, Q38, Q39, Q40, Q41, Q42, Q43, Q44]), "operationType" : NewBodyOperationType.REMOVE, "oppositeDirection" : true, "depth" : 25.4 * mm});
        }
        {
            var Q0;
            Q0=makeQuery(id+"F2.imprint","IMPRINT",FACE,{"disambiguationData":[TD([[makeQuery(id+"F2.imprint","IMPRINT",EDGE,{"derivedFrom":sQuery(id+"F2.wireOp",EDGE,"E9")}),1.0]])]});
            extrude(context, id + "F6", {"entities" : qUnion([Q0]), "operationType" : NewBodyOperationType.REMOVE, "oppositeDirection" : true, "depth" : 25.4 * mm});
        }
        {
            var Q0;
            Q0=makeQuery(id+"F1.opExtrude","CAP_FACE",FACE,{"disambiguationData":[OSD([sQuery(id+"F0.wireOp",EDGE,"E0")])],"isStart":true});
            var sketch = newSketch(context, id + "F4", { "sketchPlane" : qUnion([Q0])});
            skLineSegment(sketch, "E10", {"start": v(0, 0) * mm, "end": v(-47.08, 0) * mm});
            skCircle(sketch, "E11", {"center": v(-16.53, 0) * mm, "radius": 2.56 * mm});
            skSolve(sketch);
        }
        {
            var Q0;
            Q0 = qSketchRegion(id + "F4", true);
            extrude(context, id + "F5", {"entities" : qUnion([Q0]), "operationType" : NewBodyOperationType.REMOVE, "endBound" : BoundingType.UP_TO_NEXT, "oppositeDirection" : true, "depth" : 25.4 * mm});
        }
    });
